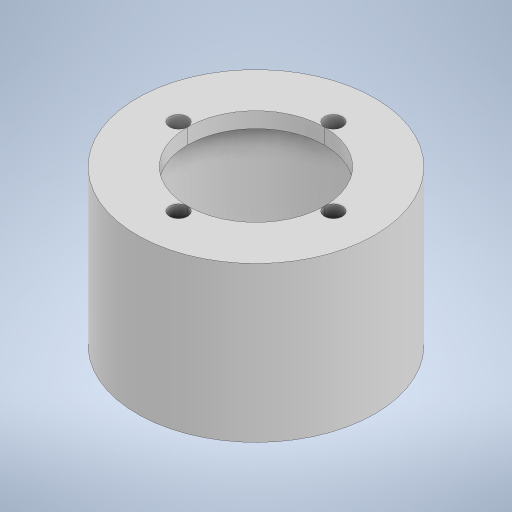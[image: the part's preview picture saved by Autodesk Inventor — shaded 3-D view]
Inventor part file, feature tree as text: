
AUTODESK INVENTOR PART (.ipt)
format: ipt  version: 2024 (Build 280153020, 153B)  size: 224,256 bytes
history: native  units: in
note: dims shown in document units (in); Inventor stores cm internally (conversion verified against a paired STEP export)
features: extrude x2, sketch x2
ambient origin geometry x8: Origin, YZ Plane, XZ Plane, XY Plane, X Axis, Y Axis, Z Axis, Center Point
bodies: Solid1 (feature_tree)
feature tree (4):
  extrude  "Extrusion1"  Depth=1.1811in
  extrude  "Extrusion2"  Depth=1.1811in
  sketch  "Sketch1"  dims[d0=1.5748in d1=1.1811in]
  sketch  "Sketch2"  dims[d2=0.1378in d3=0.1378in d4=0.1378in d5=0.1378in d6=0.1181in d7=0.0in d8=1.811in d9=1.1811in d10=0.0in]
